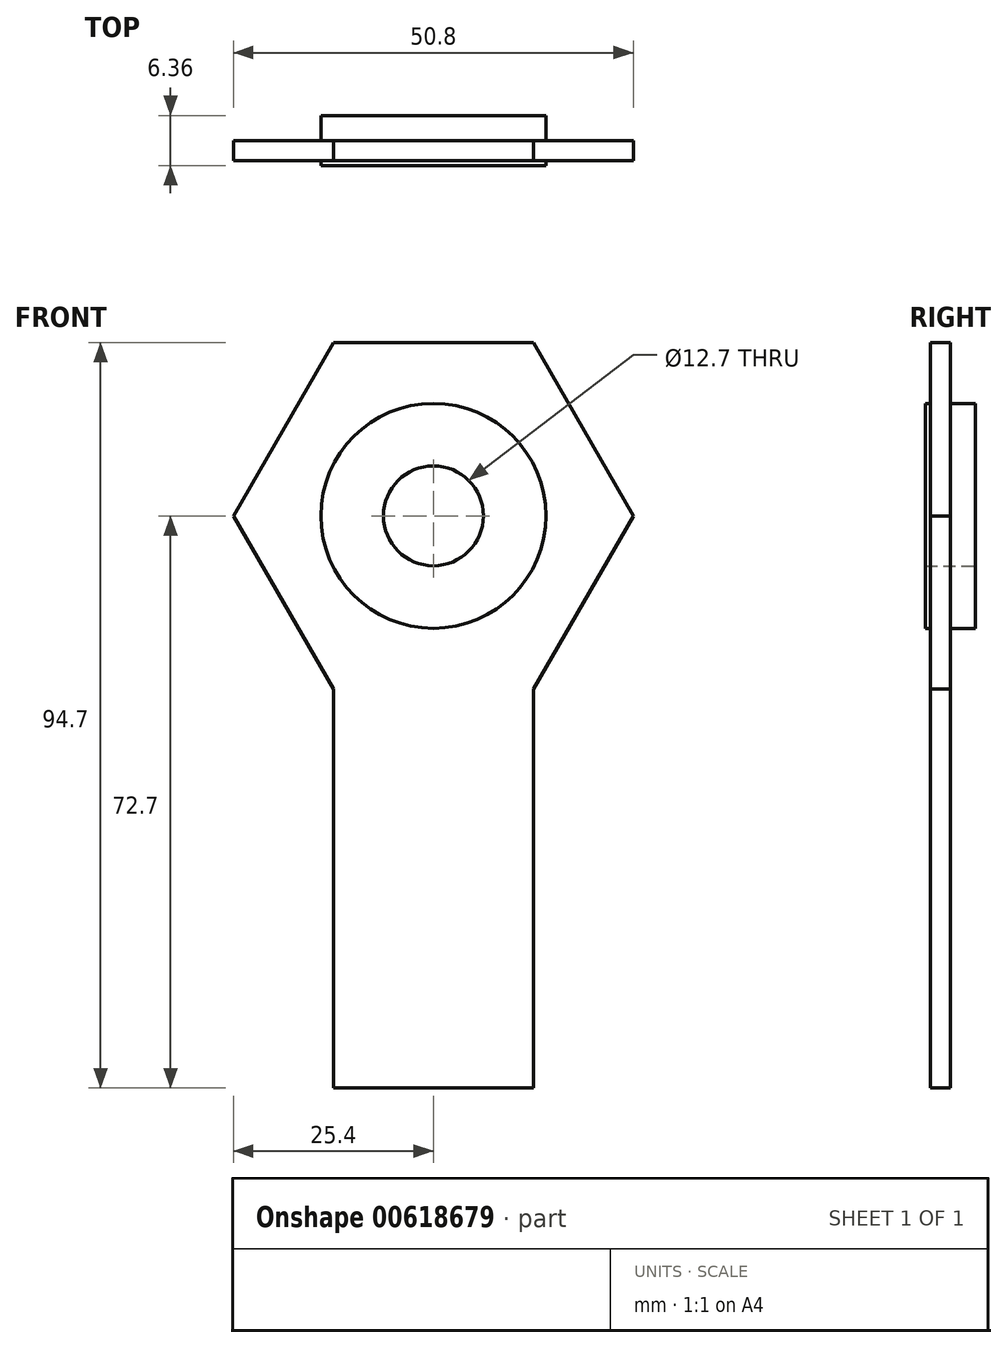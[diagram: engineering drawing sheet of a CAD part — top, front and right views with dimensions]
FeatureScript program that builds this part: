
annotation { "Feature Type Name" : "Feature", "Feature Type Description" : "" }
export const myFeature = defineFeature(function(context is Context, id is Id, definition is map)
    precondition{}
    {
        {
            var Q0;
            Q0=qCreatedBy(makeId("Front.planeOp"),FACE);
            var sketch = newSketch(context, id + "F0", { "sketchPlane" : qUnion([Q0])});
            skCircle(sketch, "E0.cCircle", {"center": v(0, 0) * mm, "radius": 22 * mm, "construction": true});
            skLineSegment(sketch, "E0.0", {"start": v(-12.7, 22) * mm, "end": v(12.7, 22) * mm});
            skLineSegment(sketch, "E0.1", {"start": v(12.7, 22) * mm, "end": v(25.4, 0) * mm});
            skLineSegment(sketch, "E0.2", {"start": v(25.4, 0) * mm, "end": v(12.7, -22) * mm});
            skLineSegment(sketch, "E0.3", {"start": v(12.7, -22) * mm, "end": v(-12.7, -22) * mm});
            skLineSegment(sketch, "E0.4", {"start": v(-12.7, -22) * mm, "end": v(-25.4, 0) * mm});
            skLineSegment(sketch, "E0.5", {"start": v(-25.4, 0) * mm, "end": v(-12.7, 22) * mm});
            skPoint(sketch, "E0.0.midPoint", {"position": v(0, 22) * mm});
            skCircle(sketch, "E1", {"center": v(0, 0) * mm, "radius": 14.29 * mm});
            skCircle(sketch, "E2", {"center": v(0, 0) * mm, "radius": 6.35 * mm});
            skLineSegment(sketch, "E3", {"start": v(-12.7, -22) * mm, "end": v(-12.7, -72.7) * mm});
            skLineSegment(sketch, "E4", {"start": v(12.7, -22) * mm, "end": v(12.7, -72.7) * mm});
            skLineSegment(sketch, "E5", {"start": v(-12.7, -72.7) * mm, "end": v(12.7, -72.7) * mm});
            skSolve(sketch);
        }
        {
            var Q0;
            Q0=makeQuery(id+"F0.imprint","IMPRINT",FACE,{"disambiguationData":[TD([[makeQuery(id+"F0.imprint","IMPRINT",EDGE,{"derivedFrom":sQuery(id+"F0.wireOp",EDGE,"E0.0")}),-1.0]])]});
            var Q1;
            Q1=makeQuery(id+"F0.imprint","IMPRINT",FACE,{"disambiguationData":[TD([[makeQuery(id+"F0.imprint","IMPRINT",EDGE,{"derivedFrom":sQuery(id+"F0.wireOp",EDGE,"E0.3")}),1.0]])]});
            extrude(context, id + "F1", {"entities" : qUnion([Q0, Q1]), "depth" : 2.54 * mm, "offsetDistance" : 25.4 * mm});
        }
        {
            var Q0;
            Q0=makeQuery(id+"F0.imprint","IMPRINT",FACE,{"disambiguationData":[TD([[makeQuery(id+"F0.imprint","IMPRINT",EDGE,{"derivedFrom":sQuery(id+"F0.wireOp",EDGE,"E1")}),1.0]])]});
            extrude(context, id + "F2", {"entities" : qUnion([Q0]), "operationType" : NewBodyOperationType.ADD, "endBound" : BoundingType.SYMMETRIC, "depth" : 6.35 * mm, "offsetDistance" : 25.4 * mm});
        }
    });
